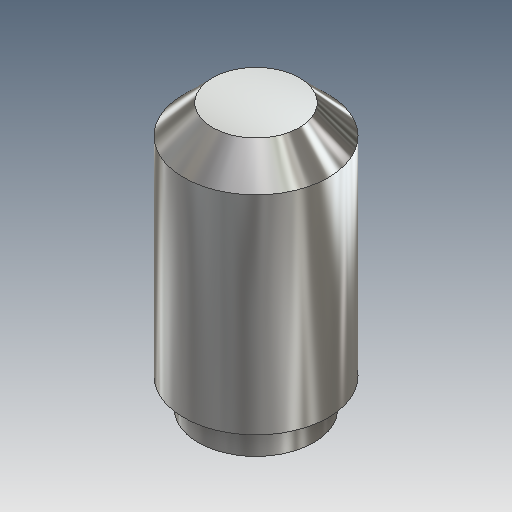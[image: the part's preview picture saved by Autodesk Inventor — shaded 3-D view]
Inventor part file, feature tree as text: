
AUTODESK INVENTOR PART (.ipt)
format: ipt  version: 2019.4 (Build 234330000, 330)  size: 156,672 bytes
history: native  units: mm
features: sketch x2, extrude x2, plane x1, chamfer x1, projected_geometry x1
ambient origin geometry x8: Origin, YZ Plane, XZ Plane, XY Plane, X Axis, Y Axis, Z Axis, Center Point
bodies: Volumenkörper1 (feature_tree)
feature tree (7):
  sketch  "Skizze1"  dims[d0=41.0mm d1=0.0mm d2=5.0mm d3=2.0mm d4=45.0deg]
  plane  "Arbeitsebene1"
  extrude  "Extrusion1"  Depth=5.0mm TaperAngle=45.0deg
  chamfer  "Fase1"  Distance=5.0mm
  extrude  "Extrusion2"  Depth=5.0mm
  sketch  "Sketch2"  dims[d5=20.0mm d6=5.0mm d7=0.0mm d8=25.0mm]
  projected_geometry  "Projected Loop1"
